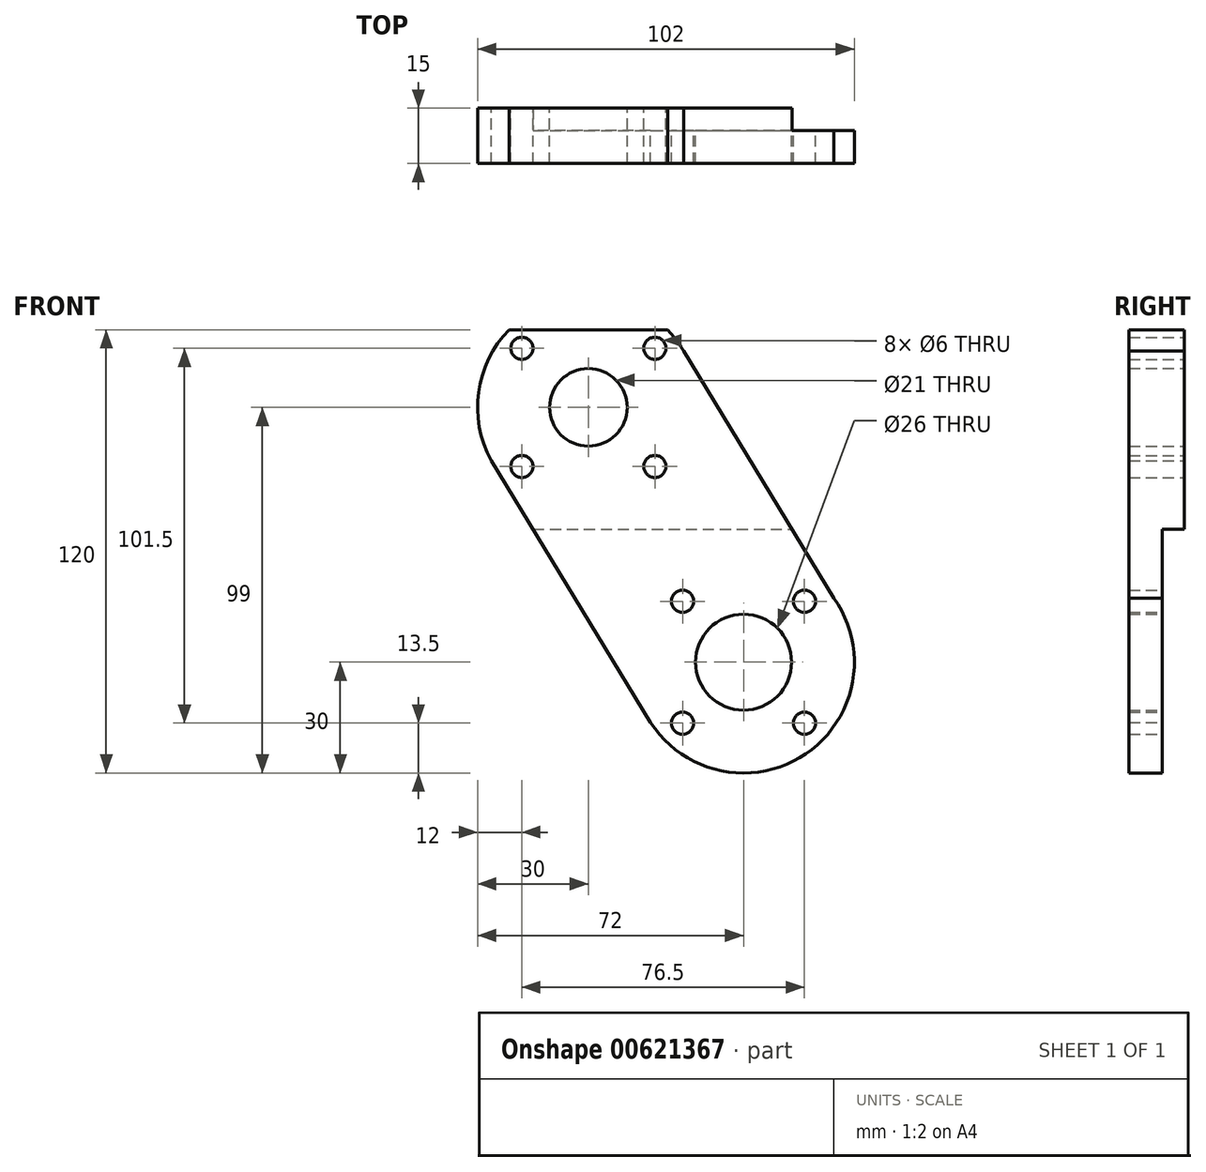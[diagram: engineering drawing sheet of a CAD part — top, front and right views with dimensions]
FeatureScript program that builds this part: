
annotation { "Feature Type Name" : "Feature", "Feature Type Description" : "" }
export const myFeature = defineFeature(function(context is Context, id is Id, definition is map)
    precondition{}
    {
        {
            var Q0;
            Q0=qCreatedBy(makeId("Front.planeOp"),FACE);
            var sketch = newSketch(context, id + "F0", { "sketchPlane" : qUnion([Q0])});
            skCircle(sketch, "E0", {"center": v(0, 0) * mm, "radius": 13 * mm});
            skArc(sketch, "E1", {"start": v(-25.16, -16.35) * mm, "mid": v(16.87, -24.8) * mm, "end": v(24.44, 17.4) * mm});
            skLineSegment(sketch, "E2", {"start": v(-16.5, -16.5) * mm, "end": v(16.5, -16.5) * mm, "construction": true});
            skLineSegment(sketch, "E3", {"start": v(16.5, -16.5) * mm, "end": v(16.5, 16.5) * mm, "construction": true});
            skLineSegment(sketch, "E4.trimOffspring", {"start": v(-16.5, 16.5) * mm, "end": v(-16.5, -16.5) * mm, "construction": true});
            skLineSegment(sketch, "E5.trimOffspring", {"start": v(-16.5, 16.5) * mm, "end": v(16.5, 16.5) * mm, "construction": true});
            skCircle(sketch, "E6", {"center": v(-16.5, 16.5) * mm, "radius": 3 * mm});
            skCircle(sketch, "E7", {"center": v(16.5, 16.5) * mm, "radius": 3 * mm});
            skCircle(sketch, "E8", {"center": v(-16.5, -16.5) * mm, "radius": 3 * mm});
            skCircle(sketch, "E9", {"center": v(16.5, -16.5) * mm, "radius": 3 * mm});
            skLineSegment(sketch, "E10", {"start": v(-42, 79.1) * mm, "end": v(-42, -6.08) * mm, "construction": true});
            skCircle(sketch, "E11", {"center": v(-42, 69) * mm, "radius": 10.5 * mm});
            skLineSegment(sketch, "E12", {"start": v(-60, 53) * mm, "end": v(-24, 53) * mm, "construction": true});
            skLineSegment(sketch, "E13", {"start": v(-24, 53) * mm, "end": v(-24, 85) * mm, "construction": true});
            skLineSegment(sketch, "E14", {"start": v(-24, 85) * mm, "end": v(-60, 85) * mm, "construction": true});
            skLineSegment(sketch, "E15", {"start": v(-60, 85) * mm, "end": v(-60, 49.23) * mm, "construction": true});
            skCircle(sketch, "E16", {"center": v(-60, 85) * mm, "radius": 3 * mm});
            skCircle(sketch, "E17", {"center": v(-24, 85) * mm, "radius": 3 * mm});
            skCircle(sketch, "E18", {"center": v(-24, 53) * mm, "radius": 3 * mm});
            skArc(sketch, "E19", {"start": v(-16.18, 84.27) * mm, "mid": v(-18.2, 87.27) * mm, "end": v(-20.58, 90) * mm});
            skLineSegment(sketch, "E20", {"start": v(-16.18, 84.27) * mm, "end": v(24.44, 17.4) * mm});
            skLineSegment(sketch, "E21", {"start": v(-25.16, -16.35) * mm, "end": v(-68.32, 54.6) * mm});
            skLineSegment(sketch, "E22", {"start": v(-77.1, 90) * mm, "end": v(31.4, 90) * mm, "construction": true});
            skLineSegment(sketch, "E23", {"start": v(-63.42, 90) * mm, "end": v(-20.58, 90) * mm});
            skArc(sketch, "E24.trimOffspring", {"start": v(-63.42, 90) * mm, "mid": v(-71.72, 73.1) * mm, "end": v(-68.32, 54.6) * mm});
            skCircle(sketch, "E25", {"center": v(0, 0) * mm, "radius": 81 * mm, "construction": true});
            skCircle(sketch, "E26", {"center": v(-60, 53) * mm, "radius": 3 * mm});
            skSolve(sketch);
        }
        {
            var Q0;
            Q0=makeQuery(id+"F0.imprint","IMPRINT",FACE,{"disambiguationData":[TD([[makeQuery(id+"F0.imprint","IMPRINT",EDGE,{"derivedFrom":sQuery(id+"F0.wireOp",EDGE,"E0")}),-1.0]])]});
            extrude(context, id + "F1", {"entities" : qUnion([Q0]), "depth" : 9 * mm, "offsetDistance" : 25 * mm});
        }
        {
            var Q0;
            Q0=makeQuery(id+"F1.opExtrude","CAP_FACE",FACE,{"disambiguationData":[OSD([sQuery(id+"F0.wireOp",EDGE,"E0"),sQuery(id+"F0.wireOp",EDGE,"E1"),sQuery(id+"F0.wireOp",EDGE,"E6"),sQuery(id+"F0.wireOp",EDGE,"E7"),sQuery(id+"F0.wireOp",EDGE,"E8"),sQuery(id+"F0.wireOp",EDGE,"E9"),sQuery(id+"F0.wireOp",EDGE,"E11"),sQuery(id+"F0.wireOp",EDGE,"E16"),sQuery(id+"F0.wireOp",EDGE,"E17"),sQuery(id+"F0.wireOp",EDGE,"E18"),sQuery(id+"F0.wireOp",EDGE,"E19"),sQuery(id+"F0.wireOp",EDGE,"E20"),sQuery(id+"F0.wireOp",EDGE,"E21"),sQuery(id+"F0.wireOp",EDGE,"E23"),sQuery(id+"F0.wireOp",EDGE,"E24.trimOffspring"),sQuery(id+"F0.wireOp",EDGE,"E26")])],"isStart":true});
            var sketch = newSketch(context, id + "F2", { "sketchPlane" : qUnion([Q0])});
            skLineSegment(sketch, "E27", {"start": v(57, 36) * mm, "end": v(-13.14, 36) * mm});
            skSolve(sketch);
        }
        {
            var Q0;
            {var subQ2=sQuery(id+"F2.wireOp",EDGE,"E27");Q0=makeQuery(id+"F2.imprint","IMPRINT",FACE,{"disambiguationData":[TD([[makeQuery(id+"F2.imprint","IMPRINT",EDGE,{"derivedFrom":subQ2}),-1.0]])]});}
            extrude(context, id + "F3", {"entities" : qUnion([Q0]), "operationType" : NewBodyOperationType.ADD, "depth" : 6 * mm, "offsetDistance" : 25 * mm});
        }
    });
